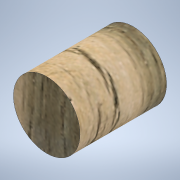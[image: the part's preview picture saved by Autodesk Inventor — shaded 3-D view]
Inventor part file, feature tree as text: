
AUTODESK INVENTOR PART (.ipt)
format: ipt  version: 2022.4 (Build 264492010, 492A)  size: 125,952 bytes
history: native  units: mm
features: other x1, extrude x1, sketch x1
ambient origin geometry x8: Origin, YZ Plane, XZ Plane, XY Plane, X Axis, Y Axis, Z Axis, Center Point
bodies: Body1 (feature_tree)
feature tree (3):
  other  "Sólido1"
  extrude  "Extrusión1"  Depth=26.0mm TaperAngle=0.0deg
  sketch  "Boceto1"  dims[d0=20.0mm d1=26.0mm d2=0.0mm]
